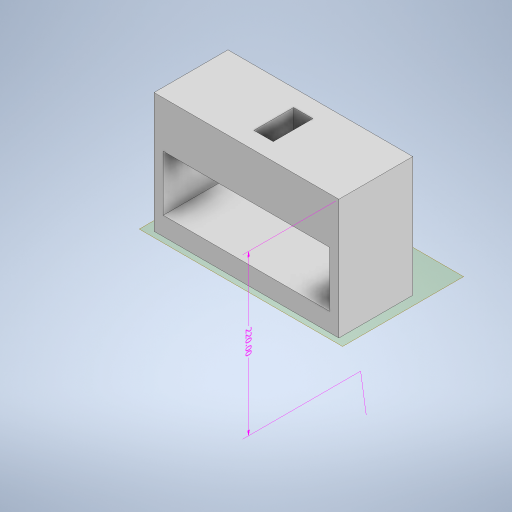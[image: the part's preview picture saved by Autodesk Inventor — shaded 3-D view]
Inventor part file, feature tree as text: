
AUTODESK INVENTOR PART (.ipt)
format: ipt  version: 2023 (Build 270158000, 158)  size: 308,736 bytes
history: native  units: mm
features: extrude x6, sketch x6, other x5, plane x3, split x1
ambient origin geometry x8: Origin, YZ Plane, XZ Plane, XY Plane, X Axis, Y Axis, Z Axis, Center Point
bodies: Body1 (feature_tree), Body2 (feature_tree)
feature tree (21):
  other  "Sólido1"
  other  "Anotaciones"
  extrude  "Extrusión1"  Depth=80.0mm
  extrude  "Extrusión2"  Depth=180.0mm
  extrude  "Extrusión3"  Depth=20.0mm
  extrude  "Extrusión4"  Depth=21.0mm
  plane  "Plano de trabajo1"
  extrude  "Extrusión6"  Depth=20.0mm
  plane  "Plano de trabajo3"
  extrude  "Extrusión7"  [1 undecoded]
  plane  "Plano de trabajo4"
  split  "Dividir1"
  other  "Suprimir cara4"
  sketch  "Boceto1"  dims[d0=200.0mm d1=80.0mm]
  sketch  "Boceto2"  dims[d2=130.0mm d3=0.0mm d4=180.0mm]
  sketch  "Boceto3"  dims[d5=60.0mm d6=20.0mm]
  sketch  "Boceto4"  dims[d7=60.0mm d8=0.0mm d9=21.0mm d10=43.0mm]
  sketch  "Boceto7"  dims[d11=43.0mm d12=0.0mm d13=20.0mm]
  other  "Sólido3"
  sketch  "Boceto10"  dims[d14=90.0mm d15=0.0mm d16=-90.0mm d28=20.0mm d29=20.0mm d30=30.0mm d31=30.0mm d32=20.0mm d33=35.0mm d34=35.0mm d35=69.0mm d36=10.0mm d37=0.0mm d45=1.5mm d50=10.0mm d51=0.0mm d52=10.0mm d53=89.5mm d54=90.0deg d38=3.166395mm d39=4.283575mm d40=220.0mm]
  other  "Cota lineal 1"
note: 1 required parameter value undecoded (feature->parameter linkage not recoverable at this tier; creation-order binding heuristic only, values carry confidence <= 0.55)
